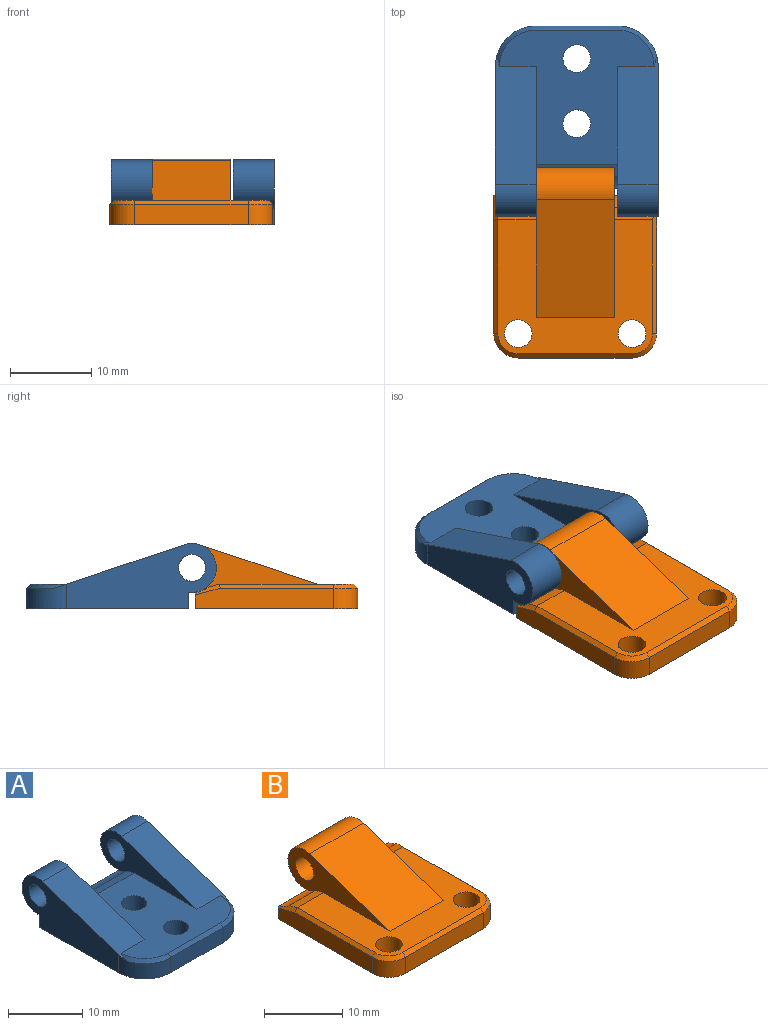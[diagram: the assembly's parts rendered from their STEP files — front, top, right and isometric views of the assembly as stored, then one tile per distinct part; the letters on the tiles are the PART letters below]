
ASSEMBLY  parts=2 mates=1
PART A: 23 faces, bbox 20x23.4x8 mm
  f0: plane 10x1.5mm, normal (0,0.29,0.96), area 15.7mm2, adj f1,f13,f14,f22
  f1: plane 19x16.5mm, normal (0,0,1), area 178.7mm2, adj f0,f3,f10,f13,f14,f15,f16,f19
  f2: cylinder r=3mm len=6mm, axis (-1,0,0), area 54mm2, adj f3,f5,f8,f14
  f3: plane 15.94x5.35mm, normal (0,-0.32,0.95), area 76.6mm2, adj f1,f2,f8,f14,f18,f21
  f4: cylinder r=1.65mm len=5mm, axis (-1,0,0), area 51.8mm2, adj f8,f14
  f5: plane 20x2.03mm, normal (0,1,0), area 39.5mm2, adj f2,f6,f8,f9,f11,f13,f14,f22
  f6: plane 18.4x8mm, normal (-1,0,0), area 90.7mm2, adj f5,f9,f10,f11,f12,f17
  f7: plane 10x2.5mm, normal (0,-1,0), area 25mm2, adj f9,f17,f18,f20
  f8: plane 18.4x8mm, normal (1,0,0), area 90.7mm2, adj f2,f3,f4,f5,f9,f18
  f9: plane 20x20mm, normal (0,0,-1), area 371.1mm2, adj f5,f6,f7,f8,f15,f16,f17,f18
  f10: plane 15.94x5.35mm, normal (0,-0.32,0.95), area 76.6mm2, adj f1,f6,f11,f13,f17,f19
  f11: cylinder r=3mm len=6mm, axis (-1,0,0), area 54mm2, adj f5,f6,f10,f13
  f12: cylinder r=1.65mm len=5mm, axis (-1,0,0), area 51.8mm2, adj f6,f13
  f13: plane 18.4x6.07mm, normal (1,0,0), area 47.3mm2, adj f0,f1,f5,f10,f11,f12,f22
  f14: plane 18.4x6.07mm, normal (-1,0,0), area 47.3mm2, adj f0,f1,f2,f3,f4,f5,f22
  f15: cylinder r=1.7mm len=3.4mm, axis (0,0,1), area 32mm2, adj f1,f9
  f16: cylinder r=1.7mm len=3.4mm, axis (0,0,1), area 32mm2, adj f1,f9
  f17: cylinder r=5mm len=5mm, axis (0,0,-1), area 20mm2, adj f6,f7,f9,f10,f19
  f18: cylinder r=5mm len=5mm, axis (0,0,1), area 20mm2, adj f3,f7,f8,f9,f21
  f19: cone r=4.5mm half-angle=45deg, axis (0,0,-1), area 4.7mm2, adj f1,f10,f17,f20
  f20: plane 10x0.5mm, normal (0,-0.71,0.71), area 7.1mm2, adj f1,f7,f19,f21
  f21: cone r=4.5mm half-angle=45deg, axis (0,0,-1), area 4.7mm2, adj f1,f3,f18,f20
  f22: cylinder r=3.1mm len=10mm, axis (1,0,0), area 16.4mm2, adj f0,f5,f13,f14
PART B: 25 faces, bbox 20x23.4x8 mm
  f0: plane 20x2.03mm, normal (0,1,0), area 39.5mm2, adj f4,f5,f7,f8,f10,f11,f22,f23
  f1: plane 5.15x1.5mm, normal (0,0.29,0.96), area 7.7mm2, adj f3,f10,f17,f24
  f2: plane 4.7x1.41mm, normal (0,0.26,0.97), area 6.9mm2, adj f3,f11,f22,f23
  f3: plane 19x16.5mm, normal (0,0,1), area 177.5mm2, adj f1,f2,f10,f11,f12,f13,f14,f17
  f4: cylinder r=3mm len=9.6mm, axis (-1,0,0), area 103.6mm2, adj f0,f10,f11,f12
  f5: plane 17x2.5mm, normal (-1,0,0), area 41.2mm2, adj f0,f8,f15,f21,f22
  f6: plane 14x2.5mm, normal (0,-1,0), area 35mm2, adj f8,f15,f16,f19
  f7: plane 17x2.5mm, normal (1,0,0), area 42mm2, adj f0,f8,f16,f17,f24
  f8: plane 20x20mm, normal (0,0,-1), area 378mm2, adj f0,f5,f6,f7,f13,f14,f15,f16
  f9: cylinder r=1.65mm len=9.6mm, axis (-1,0,0), area 99.5mm2, adj f10,f11
  f10: plane 18.4x6.07mm, normal (1,0,0), area 47.3mm2, adj f0,f1,f3,f4,f9,f12,f24
  f11: plane 18.4x6.07mm, normal (-1,0,0), area 47.3mm2, adj f0,f2,f3,f4,f9,f12,f23
  f12: plane 14.45x9.6mm, normal (0,-0.32,0.95), area 146.3mm2, adj f3,f4,f10,f11
  f13: cylinder r=1.7mm len=3.4mm, axis (0,0,1), area 32mm2, adj f3,f8
  f14: cylinder r=1.7mm len=3.4mm, axis (0,0,1), area 32mm2, adj f3,f8
  f15: cylinder r=3mm len=3mm, axis (0,0,-1), area 11.8mm2, adj f5,f6,f8,f20
  f16: cylinder r=3mm len=3mm, axis (0,0,1), area 11.8mm2, adj f6,f7,f8,f18
  f17: plane 15.57x0.5mm, normal (0.71,0,0.71), area 10.5mm2, adj f1,f3,f7,f18,f24
  f18: cone r=2.5mm half-angle=45deg, axis (0,0,-1), area 3.1mm2, adj f3,f16,f17,f19
  f19: plane 14x0.5mm, normal (0,-0.71,0.71), area 9.9mm2, adj f3,f6,f18,f20
  f20: cone r=2.5mm half-angle=45deg, axis (0,0,-1), area 3.1mm2, adj f3,f15,f19,f21
  f21: plane 14x0.5mm, normal (-0.71,0,0.71), area 9.9mm2, adj f3,f5,f20,f22
  f22: plane 3.07x1.32mm, normal (-0.71,0.18,0.68), area 1.7mm2, adj f0,f2,f5,f21,f23
  f23: cylinder r=3.1mm len=4.99mm, axis (1,0,0), area 8.7mm2, adj f0,f2,f11,f22
  f24: cylinder r=3.1mm len=5.2mm, axis (-1,0,0), area 8.5mm2, adj f0,f1,f7,f10,f17
PLACE A rot(axis=(0,0,1),180deg) t=(-40.25,8.91,1.13)mm
PLACE B t=(1.21,-7.32,1.13)mm
MATE fastened A.f2 <-> B.f24  axis (1,0,0) through (-24.42,0.79,6.13)mm
